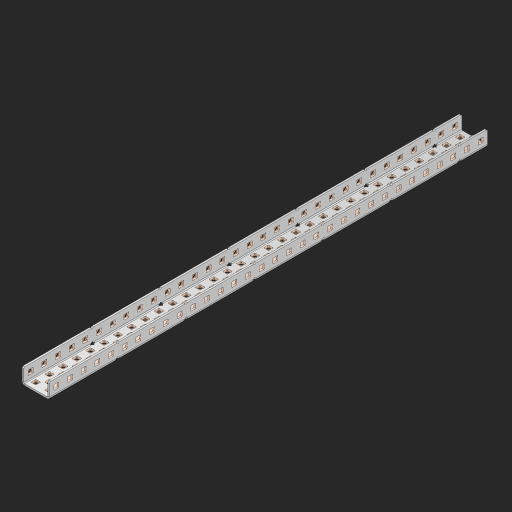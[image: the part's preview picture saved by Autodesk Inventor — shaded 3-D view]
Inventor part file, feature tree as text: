
AUTODESK INVENTOR PART (.ipt)
format: ipt  version: 2023 (Build 270158000, 158)  size: 1,975,808 bytes
history: native  units: in
note: dims shown in document units (in); Inventor stores cm internally (conversion verified against a paired STEP export)
features: other x167, extrude x158, sheet_metal_op x11, sketch x10, pattern_linear x2, mirror x1, chamfer x1
ambient origin geometry x8: Origin, YZ Plane, XZ Plane, XY Plane, X Axis, Y Axis, Z Axis, Center Point
bodies: Solid1 (feature_tree), Body (feature_tree)
feature tree (350):
  sheet_metal_op  "Flanges"
  other  "Flange Pattern Plane"
  other  "Flange Pattern Sketch"
  sheet_metal_op  "Flange Pattern"
  sheet_metal_op  "Body Pattern"
  pattern_linear  "Center Pattern"  Spacing1=0.0625in  [1 undecoded]
  other  "Arc Length"
  mirror  "Notch Mirror"
  pattern_linear  "Notch Pattern"  Spacing1=0.182in  [1 undecoded]
  chamfer  "End Chamfer"
  extrude  "Half Cut"  Depth=0.02in
  sketch  "Sketch1"  dims[d0=1.0in]
  other  "Plate1"
  sketch  "Sketch2"  dims[d1=16.0in]
  other  "Plate2"
  sheet_metal_op  "Bend1"
  sheet_metal_op  "Corner1"
  sketch  "Sketch3"  dims[d2=0.0625in]
  sketch  "Sketch7"  dims[d3=0.0625in]
  other  "Srf1"
  other  "Srf2"
  sketch  "Sketch8"  dims[d4=0.0312in]
  sketch  "Sketch9"  dims[d5=0.125in]
  other  "Srf91"
  sheet_metal_op  "Body Pattern Sketch"
  other  "Srf92"
  sketch  "Sketch13"  dims[d6=0.0625in]
  sketch  "Sketch14"  dims[d7=0.5in d8=90.0deg d9=0.0312in]
  sketch  "Sketch15"  dims[d10=0.25in]
  sketch  "Sketch16"  dims[d11=0.0625in d12=0.0625in d16=0.182in d17=0.02in d18=0.0625in d19=0.0in d20=0.25in d21=0.25in d38=12.5984in d40=0.5in d41=0.7874in d43=1.0in d46=0.172in d47=1.0in d48=0.0in d49=0.182in d50=0.02in d51=0.25in d52=0.25in d53=0.0625in d54=0.0in d55=0.172in d56=1.0in d57=0.0in d58=0.25in d60=12.5984in d62=0.5in d63=0.7874in d65=0.5in d85=0.1473in d86=0.1782in d88=0.04in d89=0.0625in d90=0.0in d91=0.04in d92=0.0491in d95=2.5in d96=0.04in d97=0.25in d98=45.0deg d99=0.25in d100=0.5in d101=0.0in d102=2.497in d106=0.182in d107=0.02in d108=0.5in d109=0.5in d110=0.0625in d111=0.0in d112=0.172in d113=0.5in d114=0.0in d117=0.5in d118=0.5in d119=0.5in]
  other  "Srf786"
  other  "Srf823"
  other  "Srf824"
  other  "Srf825"
  other  "Srf826"
  other  "Srf827"
  other  "Srf828"
  other  "Srf829"
  other  "Srf856"
  other  "Srf857"
  other  "Srf858"
  other  "Srf859"
  other  "Srf860"
  other  "Srf861"
  other  "Srf862"
  other  "Srf889"
  other  "Srf890"
  other  "Srf891"
  other  "Srf892"
  other  "Srf893"
  other  "Srf894"
  other  "Srf895"
  other  "Srf896"
  other  "Srf922"
  other  "Srf923"
  other  "Srf924"
  other  "Srf925"
  other  "Srf926"
  other  "Srf959"
  other  "Srf960"
  other  "Srf961"
  other  "Srf962"
  other  "Srf963"
  other  "Srf996"
  other  "Srf997"
  other  "Srf998"
  other  "Srf999"
  other  "Srf1000"
  other  "Srf1143"
  other  "Srf1144"
  other  "Srf1145"
  other  "Srf1146"
  other  "Srf1147"
  other  "Srf1148"
  other  "Srf1149"
  other  "Srf1150"
  other  "Srf1151"
  other  "Srf1152"
  other  "Srf1153"
  other  "Srf1154"
  other  "Srf1155"
  other  "Srf1156"
  other  "Srf1157"
  other  "Srf1158"
  other  "Srf1159"
  other  "Srf1160"
  other  "Srf1161"
  other  "Srf1162"
  other  "Srf1163"
  other  "Srf1164"
  other  "Srf1165"
  other  "Srf1166"
  other  "Srf1167"
  other  "Srf1168"
  other  "Srf1169"
  other  "Srf1170"
  other  "Srf1171"
  other  "Srf1172"
  other  "Srf1173"
  other  "Srf1174"
  other  "Srf1175"
  other  "Srf1176"
  other  "Srf1177"
  other  "Srf1178"
  other  "Srf1179"
  other  "Srf1180"
  other  "Srf1181"
  other  "Srf1182"
  other  "Srf1183"
  other  "Srf1184"
  other  "Srf1185"
  other  "Srf1186"
  other  "Srf1187"
  other  "Srf1188"
  other  "Srf1189"
  other  "Srf1190"
  other  "Srf1191"
  other  "Srf1192"
  other  "Srf1199"
  other  "Srf1200"
  other  "Srf1201"
  other  "Srf1202"
  other  "Srf1203"
  other  "Srf1204"
  other  "Srf1205"
  other  "Srf1206"
  other  "Srf1207"
  other  "Srf1208"
  other  "Srf1209"
  other  "Srf1210"
  other  "Srf1211"
  other  "Srf1212"
  other  "Srf1213"
  other  "Srf1214"
  other  "Srf1215"
  other  "Srf1216"
  other  "Srf1217"
  other  "Srf1218"
  other  "Srf1219"
  other  "Srf1220"
  other  "Srf1221"
  other  "Srf1222"
  other  "Srf1223"
  other  "Srf1224"
  other  "Srf1225"
  other  "Srf1226"
  other  "Srf1227"
  other  "Srf1228"
  other  "Srf1229"
  other  "Srf1230"
  other  "Srf1231"
  other  "Srf1232"
  other  "Srf1233"
  other  "Srf1234"
  other  "Srf1235"
  other  "Srf1236"
  other  "Srf1237"
  other  "Srf1238"
  other  "Srf1239"
  other  "Srf1240"
  other  "Srf1241"
  other  "Srf1242"
  other  "Srf1243"
  other  "Srf1244"
  other  "Srf1245"
  other  "Srf1246"
  other  "Srf1247"
  other  "Srf1248"
  other  "Srf1255"
  other  "Srf1256"
  other  "Srf1257"
  other  "Srf1258"
  other  "Srf1259"
  other  "Srf1260"
  other  "Srf1261"
  other  "Srf1262"
  other  "Srf1263"
  other  "Srf1264"
  other  "Srf1265"
  other  "Srf1266"
  other  "Srf1267"
  other  "Srf1268"
  other  "Srf1269"
  other  "Srf1270"
  other  "Srf1271"
  other  "Srf1272"
  sheet_metal_op  "Flange Stamp"
  sheet_metal_op  "Flange Circle"
  sheet_metal_op  "Body Stamp"
  sheet_metal_op  "Body Circle"
  other  "Center Stamp"
  other  "Center Circle"
  sheet_metal_op  "Notch"
  extrude  "ExtrusionSrf2"  Depth=0.0625in
  extrude  "ExtrusionSrf92"  TaperAngle=0.0deg  [1 undecoded]
  extrude  "ExtrusionSrf823"  Depth=0.5in
  extrude  "ExtrusionSrf824"  Depth=0.5in
  extrude  "ExtrusionSrf825"  Depth=0.5in
  extrude  "ExtrusionSrf826"  Depth=0.5in
  extrude  "ExtrusionSrf827"  Depth=1.0in TaperAngle=0.0deg
  extrude  "ExtrusionSrf828"  Depth=0.5in
  extrude  "ExtrusionSrf829"  Depth=0.02in
  extrude  "ExtrusionSrf856"  Depth=0.5in
  extrude  "ExtrusionSrf857"  Depth=0.5in
  extrude  "ExtrusionSrf858"  Depth=0.0625in
  extrude  "ExtrusionSrf859"  TaperAngle=0.0deg  [1 undecoded]
  extrude  "ExtrusionSrf860"  Depth=0.5in
  extrude  "ExtrusionSrf861"  Depth=1.0in TaperAngle=0.0deg
  extrude  "ExtrusionSrf862"  Depth=0.5in
  extrude  "ExtrusionSrf889"  Depth=0.5in
  extrude  "ExtrusionSrf890"  Depth=0.5in
  extrude  "ExtrusionSrf891"  Depth=0.5in
  extrude  "ExtrusionSrf892"  Depth=0.5in
  extrude  "ExtrusionSrf893"  Depth=0.5in
  extrude  "ExtrusionSrf894"  Depth=0.0625in
  extrude  "ExtrusionSrf895"  TaperAngle=0.0deg  [1 undecoded]
  extrude  "ExtrusionSrf896"  Depth=0.5in
  extrude  "ExtrusionSrf922"  Depth=0.5in
  extrude  "ExtrusionSrf923"  Depth=2.5in
  extrude  "ExtrusionSrf924"  Depth=0.5in TaperAngle=45.0deg
  extrude  "ExtrusionSrf925"  Depth=0.5in
  extrude  "ExtrusionSrf926"  Depth=0.5in TaperAngle=0.0deg
  extrude  "ExtrusionSrf959"  Depth=0.5in
  extrude  "ExtrusionSrf960"  Depth=0.5in
  extrude  "ExtrusionSrf961"  Depth=0.02in
  extrude  "ExtrusionSrf962"  Depth=0.5in
  extrude  "ExtrusionSrf963"  Depth=0.5in
  extrude  "ExtrusionSrf996"  Depth=0.0625in
  extrude  "ExtrusionSrf997"  TaperAngle=0.0deg  [1 undecoded]
  extrude  "ExtrusionSrf998"  Depth=0.5in
  extrude  "ExtrusionSrf999"  Depth=0.5in TaperAngle=0.0deg
  extrude  "ExtrusionSrf1000"  Depth=0.5in
  extrude  "ExtrusionSrf1143"  Depth=0.5in
  extrude  "ExtrusionSrf1144"  Depth=0.5in
  extrude  "ExtrusionSrf1145"  [1 undecoded]
  extrude  "ExtrusionSrf1146"  [1 undecoded]
  extrude  "ExtrusionSrf1147"  [1 undecoded]
  extrude  "ExtrusionSrf1148"  [1 undecoded]
  extrude  "ExtrusionSrf1149"  [1 undecoded]
  extrude  "ExtrusionSrf1150"  [1 undecoded]
  extrude  "ExtrusionSrf1151"  [1 undecoded]
  extrude  "ExtrusionSrf1152"  [1 undecoded]
  extrude  "ExtrusionSrf1153"  [1 undecoded]
  extrude  "ExtrusionSrf1154"  [1 undecoded]
  extrude  "ExtrusionSrf1155"  [1 undecoded]
  extrude  "ExtrusionSrf1156"  [1 undecoded]
  extrude  "ExtrusionSrf1157"  [1 undecoded]
  extrude  "ExtrusionSrf1158"  [1 undecoded]
  extrude  "ExtrusionSrf1159"  [1 undecoded]
  extrude  "ExtrusionSrf1160"  [1 undecoded]
  extrude  "ExtrusionSrf1161"  [1 undecoded]
  extrude  "ExtrusionSrf1162"  [1 undecoded]
  extrude  "ExtrusionSrf1163"  [1 undecoded]
  extrude  "ExtrusionSrf1164"  [1 undecoded]
  extrude  "ExtrusionSrf1165"  [1 undecoded]
  extrude  "ExtrusionSrf1166"  [1 undecoded]
  extrude  "ExtrusionSrf1167"  [1 undecoded]
  extrude  "ExtrusionSrf1168"  [1 undecoded]
  extrude  "ExtrusionSrf1169"  [1 undecoded]
  extrude  "ExtrusionSrf1170"  [1 undecoded]
  extrude  "ExtrusionSrf1171"  [1 undecoded]
  extrude  "ExtrusionSrf1172"  [1 undecoded]
  extrude  "ExtrusionSrf1173"  [1 undecoded]
  extrude  "ExtrusionSrf1174"  [1 undecoded]
  extrude  "ExtrusionSrf1175"  [1 undecoded]
  extrude  "ExtrusionSrf1176"  [1 undecoded]
  extrude  "ExtrusionSrf1177"  [1 undecoded]
  extrude  "ExtrusionSrf1178"  [1 undecoded]
  extrude  "ExtrusionSrf1179"  [1 undecoded]
  extrude  "ExtrusionSrf1180"  [1 undecoded]
  extrude  "ExtrusionSrf1181"  [1 undecoded]
  extrude  "ExtrusionSrf1182"  [1 undecoded]
  extrude  "ExtrusionSrf1183"  [1 undecoded]
  extrude  "ExtrusionSrf1184"  [1 undecoded]
  extrude  "ExtrusionSrf1185"  [1 undecoded]
  extrude  "ExtrusionSrf1186"  [1 undecoded]
  extrude  "ExtrusionSrf1187"  [1 undecoded]
  extrude  "ExtrusionSrf1188"  [1 undecoded]
  extrude  "ExtrusionSrf1189"  [1 undecoded]
  extrude  "ExtrusionSrf1190"  [1 undecoded]
  extrude  "ExtrusionSrf1191"  [1 undecoded]
  extrude  "ExtrusionSrf1192"  [1 undecoded]
  extrude  "ExtrusionSrf1199"  [1 undecoded]
  extrude  "ExtrusionSrf1200"  [1 undecoded]
  extrude  "ExtrusionSrf1201"  [1 undecoded]
  extrude  "ExtrusionSrf1202"  [1 undecoded]
  extrude  "ExtrusionSrf1203"  [1 undecoded]
  extrude  "ExtrusionSrf1204"  [1 undecoded]
  extrude  "ExtrusionSrf1205"  [1 undecoded]
  extrude  "ExtrusionSrf1206"  [1 undecoded]
  extrude  "ExtrusionSrf1207"  [1 undecoded]
  extrude  "ExtrusionSrf1208"  [1 undecoded]
  extrude  "ExtrusionSrf1209"  [1 undecoded]
  extrude  "ExtrusionSrf1210"  [1 undecoded]
  extrude  "ExtrusionSrf1211"  [1 undecoded]
  extrude  "ExtrusionSrf1212"  [1 undecoded]
  extrude  "ExtrusionSrf1213"  [1 undecoded]
  extrude  "ExtrusionSrf1214"  [1 undecoded]
  extrude  "ExtrusionSrf1215"  [1 undecoded]
  extrude  "ExtrusionSrf1216"  [1 undecoded]
  extrude  "ExtrusionSrf1217"  [1 undecoded]
  extrude  "ExtrusionSrf1218"  [1 undecoded]
  extrude  "ExtrusionSrf1219"  [1 undecoded]
  extrude  "ExtrusionSrf1220"  [1 undecoded]
  extrude  "ExtrusionSrf1221"  [1 undecoded]
  extrude  "ExtrusionSrf1222"  [1 undecoded]
  extrude  "ExtrusionSrf1223"  [1 undecoded]
  extrude  "ExtrusionSrf1224"  [1 undecoded]
  extrude  "ExtrusionSrf1225"  [1 undecoded]
  extrude  "ExtrusionSrf1226"  [1 undecoded]
  extrude  "ExtrusionSrf1227"  [1 undecoded]
  extrude  "ExtrusionSrf1228"  [1 undecoded]
  extrude  "ExtrusionSrf1229"  [1 undecoded]
  extrude  "ExtrusionSrf1230"  [1 undecoded]
  extrude  "ExtrusionSrf1231"  [1 undecoded]
  extrude  "ExtrusionSrf1232"  [1 undecoded]
  extrude  "ExtrusionSrf1233"  [1 undecoded]
  extrude  "ExtrusionSrf1234"  [1 undecoded]
  extrude  "ExtrusionSrf1235"  [1 undecoded]
  extrude  "ExtrusionSrf1236"  [1 undecoded]
  extrude  "ExtrusionSrf1237"  [1 undecoded]
  extrude  "ExtrusionSrf1238"  [1 undecoded]
  extrude  "ExtrusionSrf1239"  [1 undecoded]
  extrude  "ExtrusionSrf1240"  [1 undecoded]
  extrude  "ExtrusionSrf1241"  [1 undecoded]
  extrude  "ExtrusionSrf1242"  [1 undecoded]
  extrude  "ExtrusionSrf1243"  [1 undecoded]
  extrude  "ExtrusionSrf1244"  [1 undecoded]
  extrude  "ExtrusionSrf1245"  [1 undecoded]
  extrude  "ExtrusionSrf1246"  [1 undecoded]
  extrude  "ExtrusionSrf1247"  [1 undecoded]
  extrude  "ExtrusionSrf1248"  [1 undecoded]
  extrude  "ExtrusionSrf1255"  [1 undecoded]
  extrude  "ExtrusionSrf1256"  [1 undecoded]
  extrude  "ExtrusionSrf1257"  [1 undecoded]
  extrude  "ExtrusionSrf1258"  [1 undecoded]
  extrude  "ExtrusionSrf1259"  [1 undecoded]
  extrude  "ExtrusionSrf1260"  [1 undecoded]
  extrude  "ExtrusionSrf1261"  [1 undecoded]
  extrude  "ExtrusionSrf1262"  [1 undecoded]
  extrude  "ExtrusionSrf1263"  [1 undecoded]
  extrude  "ExtrusionSrf1264"  [1 undecoded]
  extrude  "ExtrusionSrf1265"  [1 undecoded]
  extrude  "ExtrusionSrf1266"  [1 undecoded]
  extrude  "ExtrusionSrf1267"  [1 undecoded]
  extrude  "ExtrusionSrf1268"  [1 undecoded]
  extrude  "ExtrusionSrf1269"  [1 undecoded]
  extrude  "ExtrusionSrf1270"  [1 undecoded]
  extrude  "ExtrusionSrf1271"  [1 undecoded]
  extrude  "ExtrusionSrf1272"  [1 undecoded]
note: 122 required parameter values undecoded (feature->parameter linkage not recoverable at this tier; creation-order binding heuristic only, values carry confidence <= 0.55)
